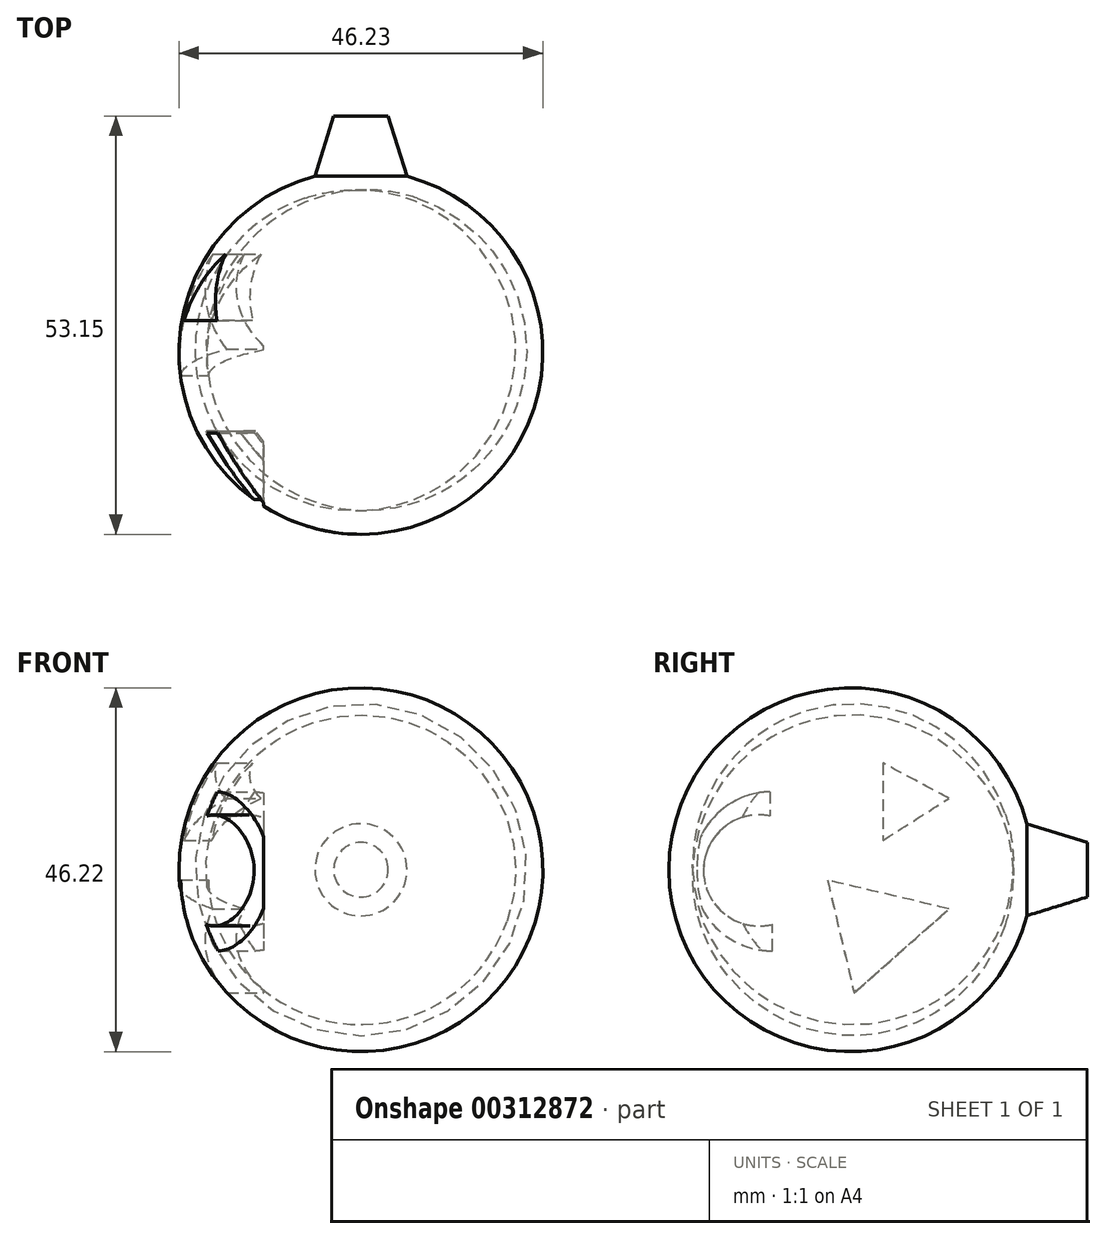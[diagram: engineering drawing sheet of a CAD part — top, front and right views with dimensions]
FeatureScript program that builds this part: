
annotation { "Feature Type Name" : "Feature", "Feature Type Description" : "" }
export const myFeature = defineFeature(function(context is Context, id is Id, definition is map)
    precondition{}
    {
        {
            var Q0;
            Q0=qCreatedBy(makeId("Top.planeOp"),FACE);
            var sketch = newSketch(context, id + "F0", { "sketchPlane" : qUnion([Q0])});
            skArc(sketch, "E0", {"start": v(-18.9, 27.05) * mm, "mid": v(-35.99, 1.74) * mm, "end": v(-13.07, -18.43) * mm});
            skLineSegment(sketch, "E1", {"start": v(-13.07, -18.43) * mm, "end": v(-13.07, -15.4) * mm});
            skLineSegment(sketch, "E2", {"start": v(-13.07, 34.72) * mm, "end": v(-16.53, 34.72) * mm});
            skLineSegment(sketch, "E3", {"start": v(-16.53, 34.72) * mm, "end": v(-18.9, 27.05) * mm});
            skArc(sketch, "E4", {"start": v(-13.07, 25.32) * mm, "mid": v(-32.73, 4.96) * mm, "end": v(-13.07, -15.4) * mm});
            skLineSegment(sketch, "E5.trimOffspring", {"start": v(-13.07, 25.32) * mm, "end": v(-13.07, 34.72) * mm});
            skSolve(sketch);
        }
        {
            var Q0;
            Q0=makeQuery(id+"F0.imprint","IMPRINT",FACE,{"disambiguationData":[TD([[makeQuery(id+"F0.imprint","IMPRINT",EDGE,{"derivedFrom":sQuery(id+"F0.wireOp",EDGE,"E0")}),1.0]])]});
            var Q1;
            Q1=sQuery(id+"F0.wireOp",EDGE,"E1");
            revolve(context, id + "F1", {"entities" : qUnion([Q0]), "axis" : qUnion([Q1]), "revolveType" : RevolveType.FULL});
        }
        {
            var Q0;
            Q0=qCreatedBy(makeId("Right.planeOp"),FACE);
            var sketch = newSketch(context, id + "F2", { "sketchPlane" : qUnion([Q0])});
            skLineSegment(sketch, "E6", {"start": v(17.17, 9.07) * mm, "end": v(8.75, 13.56) * mm});
            skLineSegment(sketch, "E7", {"start": v(8.75, 13.56) * mm, "end": v(8.75, 3.74) * mm});
            skLineSegment(sketch, "E8", {"start": v(8.75, 3.74) * mm, "end": v(17.17, 9.07) * mm});
            skLineSegment(sketch, "E9", {"start": v(17.17, -4.97) * mm, "end": v(1.73, -1.32) * mm});
            skLineSegment(sketch, "E10", {"start": v(1.73, -1.32) * mm, "end": v(5.1, -15.64) * mm});
            skLineSegment(sketch, "E11", {"start": v(5.1, -15.64) * mm, "end": v(17.17, -4.97) * mm});
            skArc(sketch, "E12", {"start": v(-5.57, 9.91) * mm, "mid": v(-15.4, -0.33) * mm, "end": v(-5.3, -10.3) * mm});
            skLineSegment(sketch, "E13", {"start": v(-5.57, 9.91) * mm, "end": v(-5.57, 6.82) * mm});
            skLineSegment(sketch, "E14", {"start": v(-5.3, -10.3) * mm, "end": v(-5.3, -6.94) * mm});
            skArc(sketch, "E15", {"start": v(-5.57, 6.82) * mm, "mid": v(-14.03, -0.23) * mm, "end": v(-5.3, -6.94) * mm});
            skSolve(sketch);
        }
        {
            var Q0;
            Q0 = qSketchRegion(id + "F2", true);
            extrude(context, id + "F3", {"entities" : qUnion([Q0]), "operationType" : NewBodyOperationType.REMOVE, "oppositeDirection" : true, "depth" : 50.8 * mm, "hasSecondDirection" : true, "secondDirectionOppositeDirection" : true, "secondDirectionDepth" : 25.4 * mm});
        }
    });
